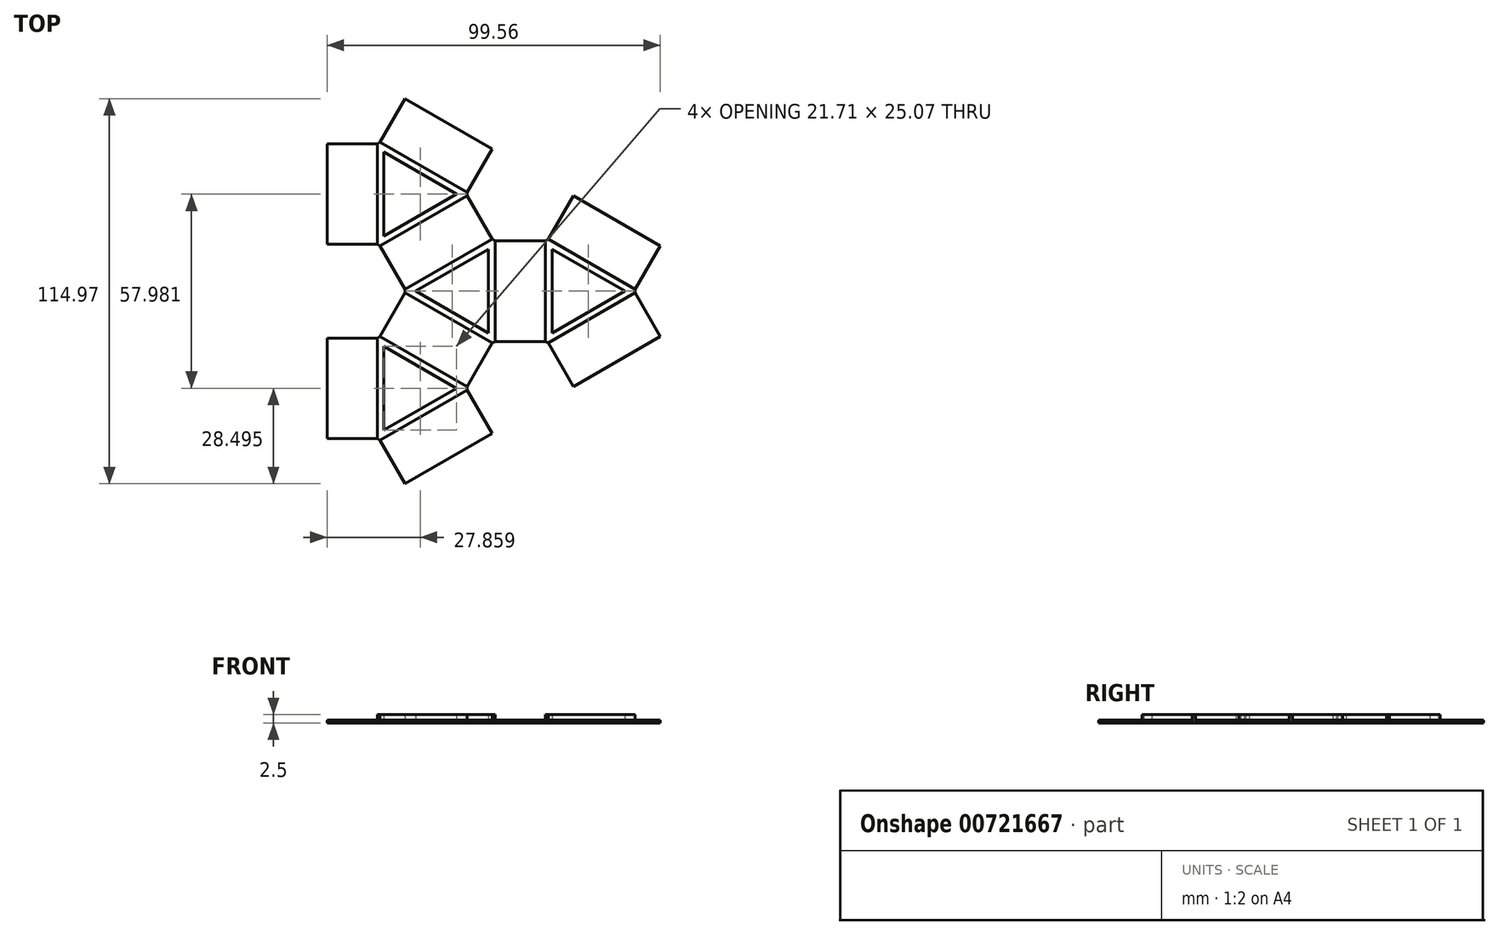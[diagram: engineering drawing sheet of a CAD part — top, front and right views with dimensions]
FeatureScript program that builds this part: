
annotation { "Feature Type Name" : "Feature", "Feature Type Description" : "" }
export const myFeature = defineFeature(function(context is Context, id is Id, definition is map)
    precondition{}
    {
        {
            var Q0;
            Q0=qCreatedBy(makeId("Top.planeOp"),FACE);
            var sketch = newSketch(context, id + "F0", { "sketchPlane" : qUnion([Q0])});
            skLineSegment(sketch, "E0.bottom", {"start": v(-8.8, 57.25) * mm, "end": v(6.2, 57.25) * mm});
            skLineSegment(sketch, "E0.top", {"start": v(-8.8, 27.25) * mm, "end": v(6.2, 27.25) * mm});
            skLineSegment(sketch, "E0.left", {"start": v(-8.8, 57.25) * mm, "end": v(-8.8, 27.25) * mm});
            skLineSegment(sketch, "E0.right", {"start": v(6.2, 57.25) * mm, "end": v(6.2, 27.25) * mm});
            skLineSegment(sketch, "E1.bottom", {"start": v(7.07, 26.75) * mm, "end": v(33.05, 41.75) * mm});
            skLineSegment(sketch, "E1.top", {"start": v(14.57, 13.76) * mm, "end": v(40.55, 28.76) * mm});
            skLineSegment(sketch, "E1.left", {"start": v(7.07, 26.75) * mm, "end": v(14.57, 13.76) * mm});
            skLineSegment(sketch, "E1.right", {"start": v(33.05, 41.75) * mm, "end": v(40.55, 28.76) * mm});
            skLineSegment(sketch, "E2.bottom", {"start": v(33.05, 42.75) * mm, "end": v(7.07, 57.75) * mm});
            skLineSegment(sketch, "E2.top", {"start": v(40.55, 55.74) * mm, "end": v(14.57, 70.74) * mm});
            skLineSegment(sketch, "E2.left", {"start": v(33.05, 42.75) * mm, "end": v(40.55, 55.74) * mm});
            skLineSegment(sketch, "E2.right", {"start": v(7.07, 57.75) * mm, "end": v(14.57, 70.74) * mm});
            skCircle(sketch, "E3.cCircle", {"center": v(15.44, 42.25) * mm, "radius": 9.24 * mm, "construction": true});
            skPoint(sketch, "E3.0.midPoint", {"position": v(6.2, 42.25) * mm});
            skPoint(sketch, "E4", {"position": v(20.06, 50.25) * mm});
            skPoint(sketch, "E5", {"position": v(20.06, 34.25) * mm});
            skPoint(sketch, "E6", {"position": v(-1.3, 27.25) * mm});
            skPoint(sketch, "E7", {"position": v(10.82, 20.25) * mm});
            skPoint(sketch, "E8", {"position": v(-1.3, 57.25) * mm});
            skLineSegment(sketch, "E9", {"start": v(-1.3, 57.25) * mm, "end": v(-1.3, 27.25) * mm, "construction": true});
            skCircle(sketch, "E10.MirrorC", {"center": v(-18.03, 42.25) * mm, "radius": 9.24 * mm, "construction": true});
            skLineSegment(sketch, "E11.MirrorCS", {"start": v(-35.64, 41.75) * mm, "end": v(-43.14, 28.76) * mm});
            skLineSegment(sketch, "E12.MirrorCS", {"start": v(-17.16, 13.76) * mm, "end": v(-43.14, 28.76) * mm});
            skLineSegment(sketch, "E13.MirrorCS", {"start": v(-9.66, 26.75) * mm, "end": v(-17.16, 13.76) * mm});
            skLineSegment(sketch, "E14.MirrorCS", {"start": v(-9.66, 26.75) * mm, "end": v(-35.64, 41.75) * mm});
            skLineSegment(sketch, "E15.MirrorCS", {"start": v(-35.64, 42.75) * mm, "end": v(-43.14, 55.74) * mm});
            skLineSegment(sketch, "E16.MirrorCS", {"start": v(-35.64, 42.75) * mm, "end": v(-9.66, 57.75) * mm});
            skLineSegment(sketch, "E17.MirrorCS", {"start": v(-9.66, 57.75) * mm, "end": v(-17.16, 70.74) * mm});
            skLineSegment(sketch, "E18.MirrorCS", {"start": v(-43.14, 55.74) * mm, "end": v(-17.16, 70.74) * mm});
            skPoint(sketch, "E19", {"position": v(-13.41, 20.25) * mm});
            skCircle(sketch, "E20", {"center": v(-1.3, 13.26) * mm, "radius": 14 * mm, "construction": true});
            skLineSegment(sketch, "E21.1.0", {"start": v(-17.16, 71.74) * mm, "end": v(-43.14, 86.74) * mm});
            skLineSegment(sketch, "E21.1.1", {"start": v(-17.16, 71.74) * mm, "end": v(-9.66, 84.73) * mm});
            skLineSegment(sketch, "E21.1.2", {"start": v(-9.66, 84.73) * mm, "end": v(-35.64, 99.73) * mm});
            skLineSegment(sketch, "E21.1.3", {"start": v(-43.14, 86.74) * mm, "end": v(-35.64, 99.73) * mm});
            skLineSegment(sketch, "E21.1.4", {"start": v(-44, 86.24) * mm, "end": v(-59, 86.24) * mm});
            skLineSegment(sketch, "E21.1.5", {"start": v(-59, 86.24) * mm, "end": v(-59, 56.24) * mm});
            skLineSegment(sketch, "E21.1.6", {"start": v(-44, 56.24) * mm, "end": v(-59, 56.24) * mm});
            skLineSegment(sketch, "E21.1.7", {"start": v(-44, 86.24) * mm, "end": v(-44, 56.24) * mm});
            skLineSegment(sketch, "E21.2.0", {"start": v(-44, 28.26) * mm, "end": v(-44, -1.74) * mm});
            skLineSegment(sketch, "E21.2.1", {"start": v(-44, 28.26) * mm, "end": v(-59, 28.26) * mm});
            skLineSegment(sketch, "E21.2.2", {"start": v(-59, 28.26) * mm, "end": v(-59, -1.74) * mm});
            skLineSegment(sketch, "E21.2.3", {"start": v(-44, -1.74) * mm, "end": v(-59, -1.74) * mm});
            skLineSegment(sketch, "E21.2.4", {"start": v(-43.14, -2.24) * mm, "end": v(-35.64, -15.24) * mm});
            skLineSegment(sketch, "E21.2.5", {"start": v(-35.64, -15.24) * mm, "end": v(-9.66, -0.24) * mm});
            skLineSegment(sketch, "E21.2.6", {"start": v(-17.16, 12.76) * mm, "end": v(-9.66, -0.24) * mm});
            skLineSegment(sketch, "E21.2.7", {"start": v(-43.14, -2.24) * mm, "end": v(-17.16, 12.76) * mm});
            skLineSegment(sketch, "E22", {"start": v(-35.64, 42.75) * mm, "end": v(-35.64, 41.75) * mm});
            skLineSegment(sketch, "E23", {"start": v(-9.66, 26.75) * mm, "end": v(-8.8, 27.25) * mm});
            skLineSegment(sketch, "E24", {"start": v(-9.66, 57.75) * mm, "end": v(-8.8, 57.25) * mm});
            skCircle(sketch, "E25.cCircle", {"center": v(-18.03, 42.25) * mm, "radius": 7.24 * mm, "construction": true});
            skLineSegment(sketch, "E25.0", {"start": v(-10.8, 54.78) * mm, "end": v(-10.8, 29.7) * mm});
            skLineSegment(sketch, "E25.1", {"start": v(-10.8, 29.7) * mm, "end": v(-32.5, 42.25) * mm});
            skLineSegment(sketch, "E25.2", {"start": v(-32.5, 42.25) * mm, "end": v(-10.8, 54.78) * mm});
            skPoint(sketch, "E25.0.midPoint", {"position": v(-10.8, 42.25) * mm});
            skLineSegment(sketch, "E26.MirrorCS", {"start": v(8.2, 54.78) * mm, "end": v(8.2, 29.7) * mm});
            skLineSegment(sketch, "E27.MirrorCS", {"start": v(29.92, 42.25) * mm, "end": v(8.2, 54.78) * mm});
            skLineSegment(sketch, "E28.MirrorCS", {"start": v(8.2, 29.7) * mm, "end": v(29.92, 42.25) * mm});
            skLineSegment(sketch, "E29.MirrorCS", {"start": v(33.05, 42.75) * mm, "end": v(33.05, 41.75) * mm});
            skLineSegment(sketch, "E30.MirrorCS", {"start": v(7.07, 26.75) * mm, "end": v(6.2, 27.25) * mm});
            skLineSegment(sketch, "E31.MirrorCS", {"start": v(7.07, 57.75) * mm, "end": v(6.2, 57.25) * mm});
            skLineSegment(sketch, "E32.1.0", {"start": v(-42, 58.7) * mm, "end": v(-20.3, 71.24) * mm});
            skLineSegment(sketch, "E32.1.1", {"start": v(-42, 83.77) * mm, "end": v(-42, 58.7) * mm});
            skLineSegment(sketch, "E32.1.2", {"start": v(-20.3, 71.24) * mm, "end": v(-42, 83.77) * mm});
            skLineSegment(sketch, "E32.1.3", {"start": v(-17.16, 71.74) * mm, "end": v(-17.16, 70.74) * mm});
            skLineSegment(sketch, "E32.1.4", {"start": v(-44, 86.24) * mm, "end": v(-43.14, 86.74) * mm});
            skLineSegment(sketch, "E32.1.5", {"start": v(-44, 56.24) * mm, "end": v(-43.14, 55.74) * mm});
            skLineSegment(sketch, "E32.2.0", {"start": v(-20.3, 13.26) * mm, "end": v(-42, 25.8) * mm});
            skLineSegment(sketch, "E32.2.1", {"start": v(-42, 0.72) * mm, "end": v(-20.3, 13.26) * mm});
            skLineSegment(sketch, "E32.2.2", {"start": v(-42, 25.8) * mm, "end": v(-42, 0.72) * mm});
            skLineSegment(sketch, "E32.2.3", {"start": v(-44, 28.26) * mm, "end": v(-43.14, 28.76) * mm});
            skLineSegment(sketch, "E32.2.4", {"start": v(-43.14, -2.24) * mm, "end": v(-44, -1.74) * mm});
            skLineSegment(sketch, "E32.2.5", {"start": v(-17.16, 12.76) * mm, "end": v(-17.16, 13.76) * mm});
            skSolve(sketch);
        }
        {
            var Q0;
            Q0=makeQuery(id+"F0.imprint","IMPRINT",FACE,{"disambiguationData":[TD([[makeQuery(id+"F0.imprint","IMPRINT",EDGE,{"derivedFrom":sQuery(id+"F0.wireOp",EDGE,"E21.2.4")}),1.0]])]});
            var Q1;
            Q1=makeQuery(id+"F0.imprint","IMPRINT",FACE,{"disambiguationData":[TD([[makeQuery(id+"F0.imprint","IMPRINT",EDGE,{"derivedFrom":sQuery(id+"F0.wireOp",EDGE,"E21.2.0")}),-1.0]])]});
            var Q2;
            Q2=makeQuery(id+"F0.imprint","IMPRINT",FACE,{"disambiguationData":[TD([[makeQuery(id+"F0.imprint","IMPRINT",EDGE,{"derivedFrom":sQuery(id+"F0.wireOp",EDGE,"E11.MirrorCS")}),1.0]])]});
            var Q3;
            Q3=makeQuery(id+"F0.imprint","IMPRINT",FACE,{"disambiguationData":[TD([[makeQuery(id+"F0.imprint","IMPRINT",EDGE,{"derivedFrom":sQuery(id+"F0.wireOp",EDGE,"E1.bottom")}),-1.0]])]});
            var Q4;
            Q4=makeQuery(id+"F0.imprint","IMPRINT",FACE,{"disambiguationData":[TD([[makeQuery(id+"F0.imprint","IMPRINT",EDGE,{"derivedFrom":sQuery(id+"F0.wireOp",EDGE,"E0.bottom")}),-1.0]])]});
            var Q5;
            Q5=makeQuery(id+"F0.imprint","IMPRINT",FACE,{"disambiguationData":[TD([[makeQuery(id+"F0.imprint","IMPRINT",EDGE,{"derivedFrom":sQuery(id+"F0.wireOp",EDGE,"E2.bottom")}),-1.0]])]});
            var Q6;
            Q6=makeQuery(id+"F0.imprint","IMPRINT",FACE,{"disambiguationData":[TD([[makeQuery(id+"F0.imprint","IMPRINT",EDGE,{"derivedFrom":sQuery(id+"F0.wireOp",EDGE,"E15.MirrorCS")}),-1.0]])]});
            var Q7;
            Q7=makeQuery(id+"F0.imprint","IMPRINT",FACE,{"disambiguationData":[TD([[makeQuery(id+"F0.imprint","IMPRINT",EDGE,{"derivedFrom":sQuery(id+"F0.wireOp",EDGE,"E21.1.0")}),-1.0]])]});
            var Q8;
            Q8=makeQuery(id+"F0.imprint","IMPRINT",FACE,{"disambiguationData":[TD([[makeQuery(id+"F0.imprint","IMPRINT",EDGE,{"derivedFrom":sQuery(id+"F0.wireOp",EDGE,"E21.1.4")}),1.0]])]});
            extrude(context, id + "F1", {"entities" : qUnion([Q0, Q1, Q2, Q3, Q4, Q5, Q6, Q7, Q8]), "depth" : 0.9 * mm, "offsetDistance" : 25 * mm});
        }
        {
            var Q0;
            Q0=makeQuery(id+"F0.imprint","IMPRINT",FACE,{"disambiguationData":[TD([[makeQuery(id+"F0.imprint","IMPRINT",EDGE,{"derivedFrom":sQuery(id+"F0.wireOp",EDGE,"E12.MirrorCS")}),1.0]])]});
            var Q1;
            Q1=makeQuery(id+"F0.imprint","IMPRINT",FACE,{"disambiguationData":[TD([[makeQuery(id+"F0.imprint","IMPRINT",EDGE,{"derivedFrom":sQuery(id+"F0.wireOp",EDGE,"E0.left")}),-1.0]])]});
            var Q2;
            Q2=makeQuery(id+"F0.imprint","IMPRINT",FACE,{"disambiguationData":[TD([[makeQuery(id+"F0.imprint","IMPRINT",EDGE,{"derivedFrom":sQuery(id+"F0.wireOp",EDGE,"E0.right")}),1.0]])]});
            var Q3;
            Q3=makeQuery(id+"F0.imprint","IMPRINT",FACE,{"disambiguationData":[TD([[makeQuery(id+"F0.imprint","IMPRINT",EDGE,{"derivedFrom":sQuery(id+"F0.wireOp",EDGE,"E18.MirrorCS")}),1.0]])]});
            extrude(context, id + "F2", {"entities" : qUnion([Q0, Q1, Q2, Q3]), "depth" : 2.5 * mm, "offsetDistance" : 25 * mm});
        }
    });
